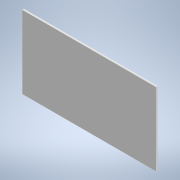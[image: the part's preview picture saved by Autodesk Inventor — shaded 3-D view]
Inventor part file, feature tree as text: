
AUTODESK INVENTOR PART (.ipt)
format: ipt  version: 2020 (Build 240168000, 168)  size: 88,576 bytes
history: native  units: mm
features: extrude x1, sketch x1
ambient origin geometry x8: Origin, YZ Plane, XZ Plane, XY Plane, X Axis, Y Axis, Z Axis, Center Point
bodies: Solid1 (feature_tree)
feature tree (2):
  extrude  "Extrusion1"  Depth=665.0mm
  sketch  "Sketch1"  dims[d0=1220.0mm d1=665.0mm d2=665.0mm d3=16.0mm d4=0.0mm]
